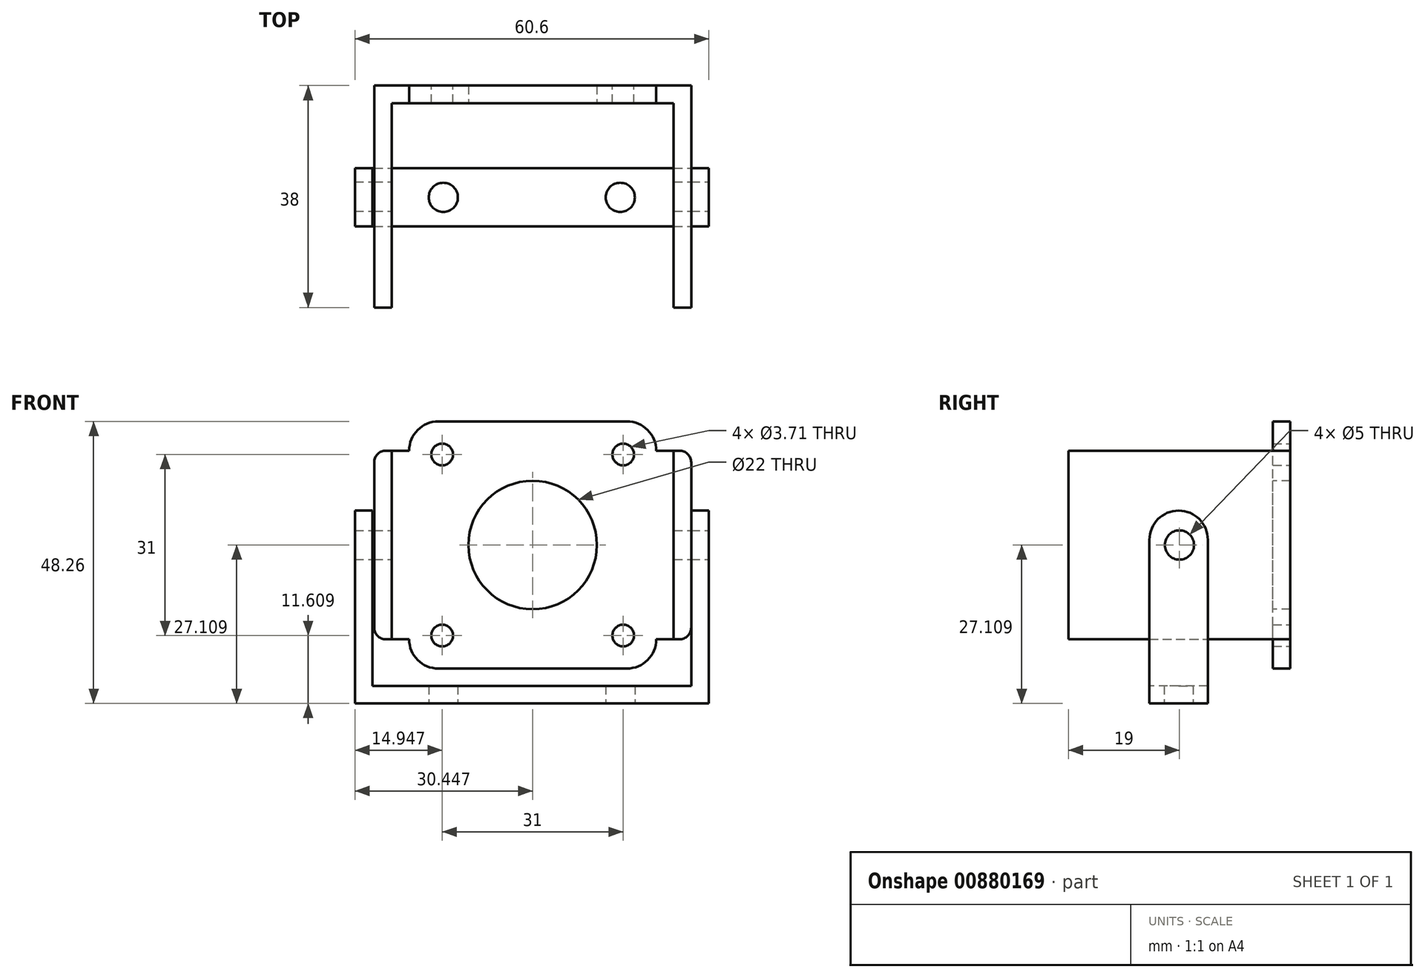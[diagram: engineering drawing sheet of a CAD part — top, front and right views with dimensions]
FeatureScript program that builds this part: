
annotation { "Feature Type Name" : "Feature", "Feature Type Description" : "" }
export const myFeature = defineFeature(function(context is Context, id is Id, definition is map)
    precondition{}
    {
        {
            var Q0;
            Q0=qCreatedBy(makeId("Front.planeOp"),FACE);
            var sketch = newSketch(context, id + "F0", { "sketchPlane" : qUnion([Q0])});
            skLineSegment(sketch, "E0.bottom", {"start": v(-12.41, 15.26) * mm, "end": v(29.89, 15.26) * mm});
            skLineSegment(sketch, "E0.top", {"start": v(-12.41, -27.04) * mm, "end": v(29.89, -27.04) * mm});
            skLineSegment(sketch, "E0.left", {"start": v(-12.41, 15.26) * mm, "end": v(-12.41, -27.04) * mm});
            skLineSegment(sketch, "E0.right", {"start": v(29.89, 15.26) * mm, "end": v(29.89, -27.04) * mm});
            skLineSegment(sketch, "E1", {"start": v(-12.41, 15.26) * mm, "end": v(-12.41, 9.6) * mm});
            skLineSegment(sketch, "E2", {"start": v(-12.41, 9.6) * mm, "end": v(-6.76, 9.6) * mm});
            skCircle(sketch, "E3", {"center": v(-6.76, 9.6) * mm, "radius": 1.85 * mm});
            skCircle(sketch, "E4.0.1.0", {"center": v(-6.76, -21.4) * mm, "radius": 1.85 * mm});
            skCircle(sketch, "E4.1.0.0", {"center": v(24.24, 9.6) * mm, "radius": 1.85 * mm});
            skCircle(sketch, "E4.1.1.0", {"center": v(24.24, -21.4) * mm, "radius": 1.85 * mm});
            skCircle(sketch, "E4.2.0.0", {"center": v(55.24, 9.6) * mm, "radius": 1.85 * mm});
            skCircle(sketch, "E4.2.1.0", {"center": v(55.24, -21.4) * mm, "radius": 1.85 * mm});
            skLineSegment(sketch, "E4.direction1", {"start": v(-6.76, 9.6) * mm, "end": v(24.24, 9.6) * mm, "construction": true});
            skLineSegment(sketch, "E4.direction2", {"start": v(-6.76, 9.6) * mm, "end": v(-6.76, -21.4) * mm, "construction": true});
            skSolve(sketch);
        }
        {
            var Q0;
            Q0=makeQuery(id+"F0.imprint","IMPRINT",FACE,{"disambiguationData":[TD([[makeQuery(id+"F0.imprint","IMPRINT",EDGE,{"derivedFrom":sQuery(id+"F0.wireOp",EDGE,"E0.bottom")}),-1.0]])]});
            extrude(context, id + "F1", {"entities" : qUnion([Q0]), "depth" : 3 * mm, "offsetDistance" : 25 * mm});
        }
        {
            var Q0;
            Q0=makeQuery(id+"F1.opExtrude","SWEPT_EDGE",EDGE,{"disambiguationData":[OSD([sQuery(id+"F0.wireOp",EDGE,"E0.bottom"),sQuery(id+"F0.wireOp",EDGE,"E0.right")])]});
            var Q1;
            Q1=makeQuery(id+"F1.opExtrude","SWEPT_EDGE",EDGE,{"disambiguationData":[OSD([sQuery(id+"F0.wireOp",EDGE,"E0.top"),sQuery(id+"F0.wireOp",EDGE,"E0.right")])]});
            var Q2;
            Q2=makeQuery(id+"F1.opExtrude","SWEPT_EDGE",EDGE,{"disambiguationData":[OSD([sQuery(id+"F0.wireOp",EDGE,"E0.bottom"),sQuery(id+"F0.wireOp",EDGE,"E1")])]});
            var Q3;
            Q3=makeQuery(id+"F1.opExtrude","SWEPT_EDGE",EDGE,{"disambiguationData":[OSD([sQuery(id+"F0.wireOp",EDGE,"E0.top"),sQuery(id+"F0.wireOp",EDGE,"E0.left")])]});
            fillet(context, id + "F2", {"entities" : qUnion([Q0, Q1, Q2, Q3]), "radius" : 5 * mm, "tangentPropagation" : true, "allowEdgeOverflow" : false});
        }
        {
            var Q0;
            Q0=makeQuery(id+"F1.opExtrude","CAP_FACE",FACE,{"disambiguationData":[OSD([sQuery(id+"F0.wireOp",EDGE,"E0.bottom"),sQuery(id+"F0.wireOp",EDGE,"E0.top"),sQuery(id+"F0.wireOp",EDGE,"E0.left"),sQuery(id+"F0.wireOp",EDGE,"E0.right"),sQuery(id+"F0.wireOp",EDGE,"E1"),sQuery(id+"F0.wireOp",EDGE,"E3"),sQuery(id+"F0.wireOp",EDGE,"E4.0.1.0"),sQuery(id+"F0.wireOp",EDGE,"E4.1.0.0"),sQuery(id+"F0.wireOp",EDGE,"E4.1.1.0")])],"isStart":true});
            var sketch = newSketch(context, id + "F3", { "sketchPlane" : qUnion([Q0])});
            skLineSegment(sketch, "E5", {"start": v(-29.89, 10.26) * mm, "end": v(-35.89, 10.26) * mm});
            skLineSegment(sketch, "E6", {"start": v(-35.89, 10.26) * mm, "end": v(-35.89, -22.04) * mm});
            skLineSegment(sketch, "E7", {"start": v(-35.89, -22.04) * mm, "end": v(-29.89, -22.04) * mm});
            skLineSegment(sketch, "E8", {"start": v(12.41, -22.04) * mm, "end": v(18.41, -22.04) * mm});
            skLineSegment(sketch, "E9", {"start": v(18.41, -22.04) * mm, "end": v(18.41, 10.26) * mm});
            skLineSegment(sketch, "E10", {"start": v(18.41, 10.26) * mm, "end": v(12.41, 10.26) * mm});
            skLineSegment(sketch, "E11", {"start": v(-32.89, 10.26) * mm, "end": v(-32.89, -22.04) * mm});
            skLineSegment(sketch, "E12", {"start": v(15.41, -22.04) * mm, "end": v(15.41, 10.26) * mm});
            skSolve(sketch);
        }
        {
            var Q0;
            {var subQ7=sQuery(id+"F3.wireOp",EDGE,"E12");Q0=makeQuery(id+"F3.imprint","IMPRINT",FACE,{"disambiguationData":[TD([[makeQuery(id+"F3.imprint","IMPRINT",EDGE,{"derivedFrom":subQ7}),1.0]])]});}
            var Q1;
            {var subQ6=sQuery(id+"F3.wireOp",EDGE,"E11");Q1=makeQuery(id+"F3.imprint","IMPRINT",FACE,{"disambiguationData":[TD([[makeQuery(id+"F3.imprint","IMPRINT",EDGE,{"derivedFrom":subQ6}),1.0]])]});}
            extrude(context, id + "F4", {"entities" : qUnion([Q0, Q1]), "operationType" : NewBodyOperationType.ADD, "oppositeDirection" : true, "depth" : 3 * mm, "offsetDistance" : 25 * mm});
        }
        {
            var Q0;
            {var subQ0=sQuery(id+"F3.wireOp",EDGE,"E9");Q0=makeQuery(id+"F3.imprint","IMPRINT",FACE,{"disambiguationData":[TD([[makeQuery(id+"F3.imprint","IMPRINT",EDGE,{"derivedFrom":subQ0}),1.0]])]});}
            var Q1;
            {var subQ0=sQuery(id+"F3.wireOp",EDGE,"E6");Q1=makeQuery(id+"F3.imprint","IMPRINT",FACE,{"disambiguationData":[TD([[makeQuery(id+"F3.imprint","IMPRINT",EDGE,{"derivedFrom":subQ0}),1.0]])]});}
            extrude(context, id + "F5", {"entities" : qUnion([Q0, Q1]), "operationType" : NewBodyOperationType.ADD, "oppositeDirection" : true, "depth" : 38 * mm, "offsetDistance" : 25 * mm});
        }
        {
            var Q0;
            Q0=makeQuery(id+"F5.opExtrude","SWEPT_EDGE",EDGE,{"disambiguationData":[OSD([sQuery(id+"F3.wireOp",EDGE,"E6"),sQuery(id+"F3.wireOp",EDGE,"E7")])]});
            var Q1;
            Q1=makeQuery(id+"F5.opExtrude","SWEPT_EDGE",EDGE,{"disambiguationData":[OSD([sQuery(id+"F3.wireOp",EDGE,"E8"),sQuery(id+"F3.wireOp",EDGE,"E9")])]});
            var Q2;
            Q2=makeQuery(id+"F5.opExtrude","SWEPT_EDGE",EDGE,{"disambiguationData":[OSD([sQuery(id+"F3.wireOp",EDGE,"E9"),sQuery(id+"F3.wireOp",EDGE,"E10")])]});
            var Q3;
            Q3=makeQuery(id+"F5.opExtrude","SWEPT_EDGE",EDGE,{"disambiguationData":[OSD([sQuery(id+"F3.wireOp",EDGE,"E5"),sQuery(id+"F3.wireOp",EDGE,"E6")])]});
            fillet(context, id + "F6", {"entities" : qUnion([Q0, Q1, Q2, Q3]), "radius" : 2 * mm, "tangentPropagation" : true, "allowEdgeOverflow" : false});
        }
        {
            var Q0;
            Q0=makeQuery(id+"F5.opExtrude","SWEPT_FACE",FACE,{"disambiguationData":[OSD([sQuery(id+"F3.wireOp",EDGE,"E6")])]});
            var sketch = newSketch(context, id + "F7", { "sketchPlane" : qUnion([Q0])});
            skLineSegment(sketch, "E13", {"start": v(-38, -5.9) * mm, "end": v(0, -5.9) * mm});
            skLineSegment(sketch, "E14", {"start": v(0, -5.9) * mm, "end": v(-19, -5.9) * mm});
            skCircle(sketch, "E15", {"center": v(-19, -5.9) * mm, "radius": 2.5 * mm});
            skSolve(sketch);
        }
        {
            var Q0;
            {var subQ0=sQuery(id+"F0.wireOp",EDGE,"E1");var subQ1=sQuery(id+"F0.wireOp",EDGE,"E0.left");var subQ2=sQuery(id+"F0.wireOp",EDGE,"E0.right");Q0=makeQuery(id+"F4.boolean.opBoolean","MERGE",FACE,{"derivedFrom":[makeQuery(id+"F1.opExtrude","CAP_FACE",FACE,{"disambiguationData":[OSD([sQuery(id+"F0.wireOp",EDGE,"E0.bottom"),sQuery(id+"F0.wireOp",EDGE,"E0.top"),subQ1,subQ2,subQ0,sQuery(id+"F0.wireOp",EDGE,"E3"),sQuery(id+"F0.wireOp",EDGE,"E4.0.1.0"),sQuery(id+"F0.wireOp",EDGE,"E4.1.0.0"),sQuery(id+"F0.wireOp",EDGE,"E4.1.1.0")])],"isStart":false}),makeQuery(id+"F4.opExtrude","CAP_FACE",FACE,{"disambiguationData":[OSD([subQ2,sQuery(id+"F3.wireOp",EDGE,"E5"),sQuery(id+"F3.wireOp",EDGE,"E7"),sQuery(id+"F3.wireOp",EDGE,"E11")])],"isStart":false}),makeQuery(id+"F4.opExtrude","CAP_FACE",FACE,{"disambiguationData":[OSD([subQ1,subQ0,sQuery(id+"F3.wireOp",EDGE,"E8"),sQuery(id+"F3.wireOp",EDGE,"E10"),sQuery(id+"F3.wireOp",EDGE,"E12")])],"isStart":false})]});}
            var sketch = newSketch(context, id + "F8", { "sketchPlane" : qUnion([Q0])});
            skCircle(sketch, "E16", {"center": v(8.74, -5.9) * mm, "radius": 11 * mm});
            skPoint(sketch, "E16.centerSnap0", {"position": v(32.89, -5.9) * mm});
            skPoint(sketch, "E16.centerSnap1", {"position": v(8.74, 15.26) * mm});
            skSolve(sketch);
        }
        {
            var Q0;
            Q0 = qSketchRegion(id + "F8", true);
            extrude(context, id + "F9", {"entities" : qUnion([Q0]), "operationType" : NewBodyOperationType.REMOVE, "endBound" : BoundingType.THROUGH_ALL, "oppositeDirection" : true, "depth" : 25 * mm, "offsetDistance" : 25 * mm});
        }
        {
            var Q0;
            Q0=makeQuery(id+"F5.opExtrude","SWEPT_FACE",FACE,{"disambiguationData":[OSD([sQuery(id+"F3.wireOp",EDGE,"E6")])]});
            var sketch = newSketch(context, id + "F10", { "sketchPlane" : qUnion([Q0])});
            skLineSegment(sketch, "E17", {"start": v(-19, -20.04) * mm, "end": v(-19, 0) * mm});
            skLineSegment(sketch, "E18", {"start": v(-19, 0) * mm, "end": v(-24.13, 0) * mm});
            skLineSegment(sketch, "E19", {"start": v(-24.13, 0) * mm, "end": v(-14.13, 0) * mm});
            skLineSegment(sketch, "E20", {"start": v(-14.13, 0) * mm, "end": v(-14.13, -30) * mm});
            skLineSegment(sketch, "E21", {"start": v(-14.13, -30) * mm, "end": v(-24.13, -30) * mm});
            skLineSegment(sketch, "E22", {"start": v(-24.13, -30) * mm, "end": v(-24.13, 0) * mm});
            skLineSegment(sketch, "E23", {"start": v(-24.13, -30) * mm, "end": v(-24.13, -33) * mm});
            skLineSegment(sketch, "E24", {"start": v(-24.13, -33) * mm, "end": v(-14.13, -33) * mm});
            skLineSegment(sketch, "E25", {"start": v(-14.13, -33) * mm, "end": v(-14.13, -30) * mm});
            skSolve(sketch);
        }
        {
            var Q0;
            Q0 = qSketchRegion(id + "F10", true);
            extrude(context, id + "F11", {"entities" : qUnion([Q0]), "depth" : 3 * mm, "offsetDistance" : 25 * mm});
        }
        {
            var Q0;
            Q0=makeQuery(id+"F11.opExtrude","SWEPT_EDGE",EDGE,{"disambiguationData":[OSD([sQuery(id+"F10.wireOp",EDGE,"E19"),sQuery(id+"F10.wireOp",EDGE,"E22")])]});
            var Q1;
            Q1=makeQuery(id+"F11.opExtrude","SWEPT_EDGE",EDGE,{"disambiguationData":[OSD([sQuery(id+"F10.wireOp",EDGE,"E19"),sQuery(id+"F10.wireOp",EDGE,"E20")])]});
            fillet(context, id + "F12", {"entities" : qUnion([Q0, Q1]), "radius" : 5 * mm, "tangentPropagation" : true, "allowEdgeOverflow" : false});
        }
        {
            var Q0;
            Q0=makeQuery(id+"F10.imprint","IMPRINT",FACE,{"disambiguationData":[TD([[makeQuery(id+"F10.imprint","IMPRINT",EDGE,{"derivedFrom":sQuery(id+"F10.wireOp",EDGE,"E21")}),1.0]])]});
            extrude(context, id + "F13", {"entities" : qUnion([Q0]), "operationType" : NewBodyOperationType.ADD, "oppositeDirection" : true, "depth" : 54.6 * mm, "offsetDistance" : 25 * mm});
        }
        {
            var Q0;
            Q0=makeQuery(id+"F13.opExtrude","CAP_FACE",FACE,{"disambiguationData":[OSD([sQuery(id+"F10.wireOp",EDGE,"E21"),sQuery(id+"F10.wireOp",EDGE,"E23"),sQuery(id+"F10.wireOp",EDGE,"E24"),sQuery(id+"F10.wireOp",EDGE,"E25")])],"isStart":false});
            var sketch = newSketch(context, id + "F14", { "sketchPlane" : qUnion([Q0])});
            skLineSegment(sketch, "E26", {"start": v(14.13, -33) * mm, "end": v(14.13, 0) * mm});
            skLineSegment(sketch, "E27", {"start": v(14.13, 0) * mm, "end": v(24.13, 0) * mm});
            skLineSegment(sketch, "E28", {"start": v(24.13, 0) * mm, "end": v(24.13, -33) * mm});
            skSolve(sketch);
        }
        {
            var Q0;
            {var subQ2=sQuery(id+"F14.wireOp",EDGE,"E27");Q0=makeQuery(id+"F14.imprint","IMPRINT",FACE,{"disambiguationData":[TD([[makeQuery(id+"F14.imprint","IMPRINT",EDGE,{"derivedFrom":subQ2}),-1.0]])]});}
            var Q1;
            {var subQ1=makeQuery(id+"F13.opExtrude","CAP_EDGE",EDGE,{"disambiguationData":[OSD([sQuery(id+"F10.wireOp",EDGE,"E21")])],"isStart":false});Q1=makeQuery(id+"F14.imprint","IMPRINT",FACE,{"disambiguationData":[TD([[makeQuery(id+"F14.imprint","IMPRINT",EDGE,{"derivedFrom":subQ1}),-1.0]])]});}
            extrude(context, id + "F15", {"entities" : qUnion([Q0, Q1]), "operationType" : NewBodyOperationType.ADD, "depth" : 3 * mm, "offsetDistance" : 25 * mm});
        }
        {
            var Q0;
            Q0 = qSketchRegion(id + "F7", true);
            extrude(context, id + "F16", {"entities" : qUnion([Q0]), "operationType" : NewBodyOperationType.REMOVE, "endBound" : BoundingType.THROUGH_ALL, "oppositeDirection" : true, "depth" : 25 * mm, "offsetDistance" : 25 * mm, "hasSecondDirection" : true, "secondDirectionBound" : SecondDirectionBoundingType.THROUGH_ALL, "secondDirectionOppositeDirection" : false, "secondDirectionDepth" : 25 * mm});
        }
        {
            var Q0;
            Q0=makeQuery(id+"F15.opExtrude","SWEPT_EDGE",EDGE,{"disambiguationData":[OSD([sQuery(id+"F14.wireOp",EDGE,"E26"),sQuery(id+"F14.wireOp",EDGE,"E27")])]});
            var Q1;
            Q1=makeQuery(id+"F15.opExtrude","SWEPT_EDGE",EDGE,{"disambiguationData":[OSD([sQuery(id+"F14.wireOp",EDGE,"E27"),sQuery(id+"F14.wireOp",EDGE,"E28")])]});
            fillet(context, id + "F17", {"entities" : qUnion([Q0, Q1]), "radius" : 5 * mm, "tangentPropagation" : true, "allowEdgeOverflow" : false});
        }
        {
            var Q0;
            {var subQ0=sQuery(id+"F10.wireOp",EDGE,"E24");Q0=makeQuery(id+"F15.boolean.opBoolean","MERGE",FACE,{"derivedFrom":[makeQuery(id+"F13.boolean.opBoolean","MERGE",FACE,{"derivedFrom":[makeQuery(id+"F11.opExtrude","SWEPT_FACE",FACE,{"disambiguationData":[OSD([subQ0])]}),makeQuery(id+"F13.opExtrude","SWEPT_FACE",FACE,{"disambiguationData":[OSD([subQ0])]})]}),makeQuery(id+"F15.opExtrude","SWEPT_FACE",FACE,{"disambiguationData":[OSD([subQ0])]})]});}
            var sketch = newSketch(context, id + "F18", { "sketchPlane" : qUnion([Q0])});
            skLineSegment(sketch, "E29", {"start": v(-21.71, 19.13) * mm, "end": v(38.89, 19.13) * mm});
            skLineSegment(sketch, "E30", {"start": v(38.89, 19.13) * mm, "end": v(8.59, 19.13) * mm});
            skLineSegment(sketch, "E31", {"start": v(8.59, 19.13) * mm, "end": v(-6.56, 19.13) * mm});
            skLineSegment(sketch, "E32", {"start": v(-6.56, 19.13) * mm, "end": v(23.74, 19.13) * mm});
            skCircle(sketch, "E33", {"center": v(-6.56, 19.13) * mm, "radius": 2.5 * mm});
            skCircle(sketch, "E34", {"center": v(23.74, 19.13) * mm, "radius": 2.5 * mm});
            skSolve(sketch);
        }
        {
            var Q0;
            Q0 = qSketchRegion(id + "F18", true);
            extrude(context, id + "F19", {"entities" : qUnion([Q0]), "operationType" : NewBodyOperationType.REMOVE, "oppositeDirection" : true, "depth" : 25 * mm, "offsetDistance" : 25 * mm});
        }
    });
